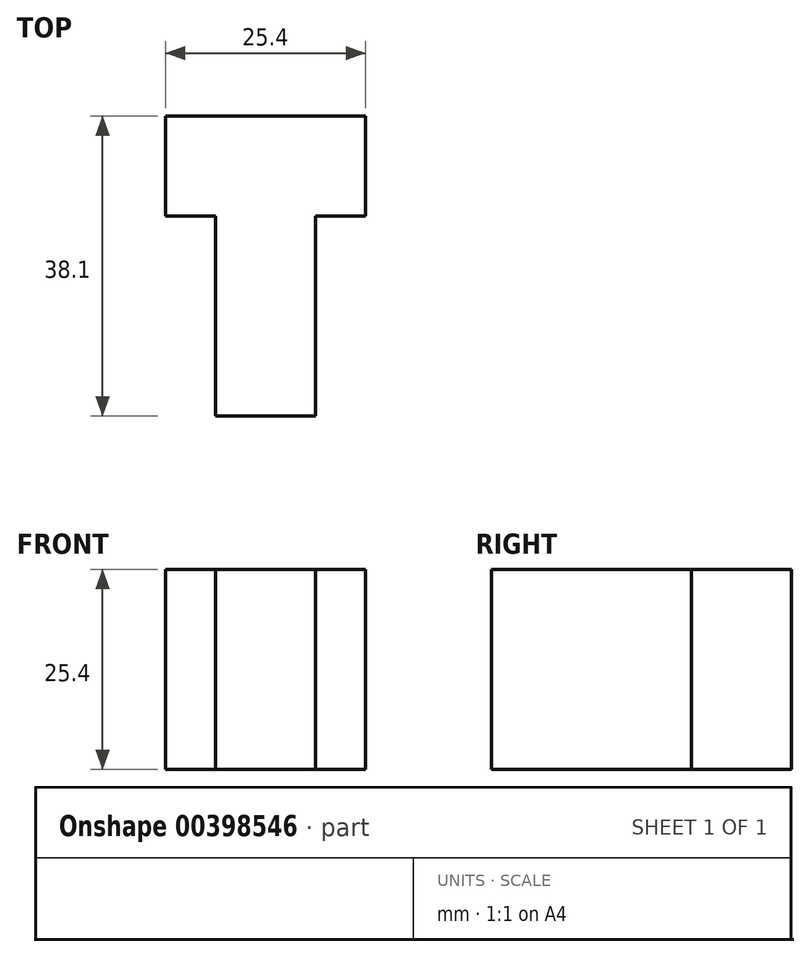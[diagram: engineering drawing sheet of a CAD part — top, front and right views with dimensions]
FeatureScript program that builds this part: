
annotation { "Feature Type Name" : "Feature", "Feature Type Description" : "" }
export const myFeature = defineFeature(function(context is Context, id is Id, definition is map)
    precondition{}
    {
        {
            var Q0;
            Q0=qCreatedBy(makeId("Top.planeOp"),FACE);
            var sketch = newSketch(context, id + "F0", { "sketchPlane" : qUnion([Q0])});
            skLineSegment(sketch, "E0", {"start": v(0, 0) * mm, "end": v(12.7, 0) * mm});
            skLineSegment(sketch, "E1", {"start": v(12.7, 0) * mm, "end": v(12.7, 25.4) * mm});
            skLineSegment(sketch, "E2", {"start": v(12.7, 25.4) * mm, "end": v(19.05, 25.4) * mm});
            skLineSegment(sketch, "E3", {"start": v(19.05, 38.1) * mm, "end": v(19.05, 25.4) * mm});
            skLineSegment(sketch, "E4", {"start": v(19.05, 38.1) * mm, "end": v(-6.35, 38.1) * mm});
            skLineSegment(sketch, "E5", {"start": v(-6.35, 25.4) * mm, "end": v(-6.35, 38.1) * mm});
            skLineSegment(sketch, "E6", {"start": v(-6.35, 25.4) * mm, "end": v(0, 25.4) * mm});
            skLineSegment(sketch, "E7", {"start": v(0, 0) * mm, "end": v(0, 25.4) * mm});
            skSolve(sketch);
        }
        {
            var Q0;
            Q0=makeQuery(id+"F0.imprint","IMPRINT",FACE,{"disambiguationData":[TD([[makeQuery(id+"F0.imprint","IMPRINT",EDGE,{"derivedFrom":sQuery(id+"F0.wireOp",EDGE,"E0")}),1.0]])]});
            extrude(context, id + "F1", {"entities" : qUnion([Q0]), "depth" : 25.4 * mm});
        }
    });
